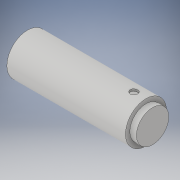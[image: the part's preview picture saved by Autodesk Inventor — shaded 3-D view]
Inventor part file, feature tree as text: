
AUTODESK INVENTOR PART (.ipt)
format: ipt  version: 2018.3 (Build 223284000, 284)  size: 122,368 bytes
history: native  units: in
note: dims shown in document units (in); Inventor stores cm internally (conversion verified against a paired STEP export)
features: sketch x2, revolve x1, extrude x1
ambient origin geometry x8: Origin, YZ Plane, XZ Plane, XY Plane, X Axis, Y Axis, Z Axis, Center Point
bodies: Solid1 (feature_tree)
feature tree (4):
  revolve  "Revolution1"  [1 undecoded]
  extrude  "Extrusion1"  Depth=0.196in
  sketch  "Sketch1"  dims[d0=1.44in d1=0.2492in]
  sketch  "Sketch2"  dims[d2=1.52in d3=0.196in d4=1.34in d5=0.224in d6=90.0deg d7=0.09in d8=1.0in d9=0.0in]
note: 1 required parameter value undecoded (feature->parameter linkage not recoverable at this tier; creation-order binding heuristic only, values carry confidence <= 0.55)
